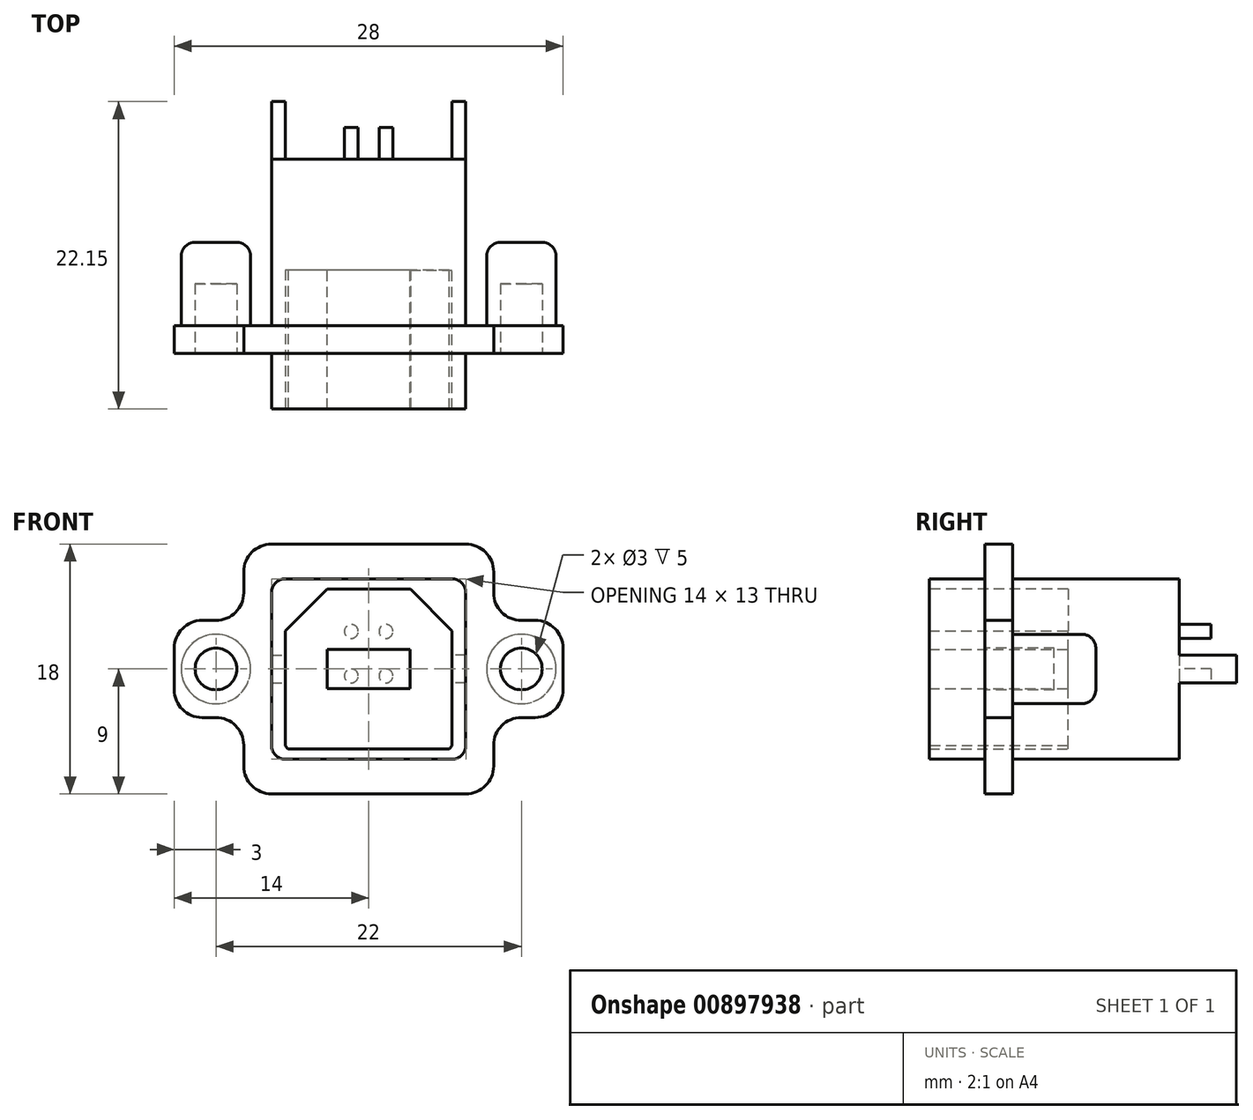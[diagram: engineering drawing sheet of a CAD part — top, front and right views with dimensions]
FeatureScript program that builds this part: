
annotation { "Feature Type Name" : "Feature", "Feature Type Description" : "" }
export const myFeature = defineFeature(function(context is Context, id is Id, definition is map)
    precondition{}
    {
        {
            var Q0;
            Q0=qCreatedBy(makeId("Front.planeOp"),FACE);
            var sketch = newSketch(context, id + "F0", { "sketchPlane" : qUnion([Q0])});
            skLineSegment(sketch, "E0.bottom", {"start": v(9, -9) * mm, "end": v(-9, -9) * mm});
            skLineSegment(sketch, "E0.top", {"start": v(9, 9) * mm, "end": v(-9, 9) * mm});
            skLineSegment(sketch, "E0.left", {"start": v(9, -9) * mm, "end": v(9, 9) * mm});
            skLineSegment(sketch, "E0.right", {"start": v(-9, -9) * mm, "end": v(-9, 9) * mm});
            skPoint(sketch, "E0.middle", {"position": v(0, 0) * mm});
            skLineSegment(sketch, "E1.bottom", {"start": v(-9, 3.5) * mm, "end": v(-14, 3.5) * mm});
            skLineSegment(sketch, "E1.top", {"start": v(-9, -3.5) * mm, "end": v(-14, -3.5) * mm});
            skLineSegment(sketch, "E1.left", {"start": v(-9, 3.5) * mm, "end": v(-9, -3.5) * mm});
            skLineSegment(sketch, "E1.right", {"start": v(-14, 3.5) * mm, "end": v(-14, -3.5) * mm});
            skLineSegment(sketch, "E2.bottom", {"start": v(9, 3.5) * mm, "end": v(14, 3.5) * mm});
            skLineSegment(sketch, "E2.top", {"start": v(9, -3.5) * mm, "end": v(14, -3.5) * mm});
            skLineSegment(sketch, "E2.left", {"start": v(9, 3.5) * mm, "end": v(9, -3.5) * mm});
            skLineSegment(sketch, "E2.right", {"start": v(14, 3.5) * mm, "end": v(14, -3.5) * mm});
            skSolve(sketch);
        }
        {
            var Q0;
            Q0 = qSketchRegion(id + "F0", true);
            extrude(context, id + "F1", {"entities" : qUnion([Q0]), "depth" : 2 * mm, "offsetDistance" : 25 * mm});
        }
        {
            var Q0;
            Q0=makeQuery(id+"F1.opExtrude","CAP_FACE",FACE,{"disambiguationData":[OSD([sQuery(id+"F0.wireOp",EDGE,"E0.bottom"),sQuery(id+"F0.wireOp",EDGE,"E0.top"),sQuery(id+"F0.wireOp",EDGE,"E0.left"),sQuery(id+"F0.wireOp",EDGE,"E0.right"),sQuery(id+"F0.wireOp",EDGE,"E1.bottom"),sQuery(id+"F0.wireOp",EDGE,"E1.top"),sQuery(id+"F0.wireOp",EDGE,"E1.right"),sQuery(id+"F0.wireOp",EDGE,"E2.bottom"),sQuery(id+"F0.wireOp",EDGE,"E2.top"),sQuery(id+"F0.wireOp",EDGE,"E2.right")])],"isStart":false});
            var sketch = newSketch(context, id + "F2", { "sketchPlane" : qUnion([Q0])});
            skLineSegment(sketch, "E3.bottom", {"start": v(7, -6.5) * mm, "end": v(-7, -6.5) * mm});
            skLineSegment(sketch, "E3.top", {"start": v(7, 6.5) * mm, "end": v(-7, 6.5) * mm});
            skLineSegment(sketch, "E3.left", {"start": v(7, -6.5) * mm, "end": v(7, 6.5) * mm});
            skLineSegment(sketch, "E3.right", {"start": v(-7, -6.5) * mm, "end": v(-7, 6.5) * mm});
            skPoint(sketch, "E3.middle", {"position": v(0, 0) * mm});
            skSolve(sketch);
        }
        {
            var Q0;
            Q0 = qSketchRegion(id + "F2", true);
            extrude(context, id + "F3", {"entities" : qUnion([Q0]), "operationType" : NewBodyOperationType.ADD, "depth" : 4 * mm, "offsetDistance" : 25 * mm});
        }
        {
            var Q0;
            Q0=makeQuery(id+"F1.opExtrude","CAP_FACE",FACE,{"disambiguationData":[OSD([sQuery(id+"F0.wireOp",EDGE,"E0.bottom"),sQuery(id+"F0.wireOp",EDGE,"E0.top"),sQuery(id+"F0.wireOp",EDGE,"E0.left"),sQuery(id+"F0.wireOp",EDGE,"E0.right"),sQuery(id+"F0.wireOp",EDGE,"E1.bottom"),sQuery(id+"F0.wireOp",EDGE,"E1.top"),sQuery(id+"F0.wireOp",EDGE,"E1.right"),sQuery(id+"F0.wireOp",EDGE,"E2.bottom"),sQuery(id+"F0.wireOp",EDGE,"E2.top"),sQuery(id+"F0.wireOp",EDGE,"E2.right")])],"isStart":true});
            var sketch = newSketch(context, id + "F4", { "sketchPlane" : qUnion([Q0])});
            skLineSegment(sketch, "E4.bottom", {"start": v(7, -6.5) * mm, "end": v(-7, -6.5) * mm});
            skLineSegment(sketch, "E4.top", {"start": v(7, 6.5) * mm, "end": v(-7, 6.5) * mm});
            skLineSegment(sketch, "E4.left", {"start": v(7, -6.5) * mm, "end": v(7, 6.5) * mm});
            skLineSegment(sketch, "E4.right", {"start": v(-7, -6.5) * mm, "end": v(-7, 6.5) * mm});
            skPoint(sketch, "E4.middle", {"position": v(0, 0) * mm});
            skSolve(sketch);
        }
        {
            var Q0;
            Q0 = qSketchRegion(id + "F4", true);
            extrude(context, id + "F5", {"entities" : qUnion([Q0]), "operationType" : NewBodyOperationType.ADD, "depth" : 12 * mm, "offsetDistance" : 25 * mm});
        }
        {
            var Q0;
            Q0=makeQuery(id+"F1.opExtrude","CAP_FACE",FACE,{"disambiguationData":[OSD([sQuery(id+"F0.wireOp",EDGE,"E0.bottom"),sQuery(id+"F0.wireOp",EDGE,"E0.top"),sQuery(id+"F0.wireOp",EDGE,"E0.left"),sQuery(id+"F0.wireOp",EDGE,"E0.right"),sQuery(id+"F0.wireOp",EDGE,"E1.bottom"),sQuery(id+"F0.wireOp",EDGE,"E1.top"),sQuery(id+"F0.wireOp",EDGE,"E1.right"),sQuery(id+"F0.wireOp",EDGE,"E2.bottom"),sQuery(id+"F0.wireOp",EDGE,"E2.top"),sQuery(id+"F0.wireOp",EDGE,"E2.right")])],"isStart":true});
            var sketch = newSketch(context, id + "F6", { "sketchPlane" : qUnion([Q0])});
            skCircle(sketch, "E5", {"center": v(11, 0) * mm, "radius": 2.5 * mm});
            skCircle(sketch, "E6", {"center": v(-11, 0) * mm, "radius": 2.5 * mm});
            skSolve(sketch);
        }
        {
            var Q0;
            Q0 = qSketchRegion(id + "F6", true);
            extrude(context, id + "F7", {"entities" : qUnion([Q0]), "operationType" : NewBodyOperationType.ADD, "depth" : 6 * mm, "offsetDistance" : 25 * mm});
        }
        {
            var Q0;
            Q0=makeQuery(id+"F1.opExtrude","CAP_FACE",FACE,{"disambiguationData":[OSD([sQuery(id+"F0.wireOp",EDGE,"E0.bottom"),sQuery(id+"F0.wireOp",EDGE,"E0.top"),sQuery(id+"F0.wireOp",EDGE,"E0.left"),sQuery(id+"F0.wireOp",EDGE,"E0.right"),sQuery(id+"F0.wireOp",EDGE,"E1.bottom"),sQuery(id+"F0.wireOp",EDGE,"E1.top"),sQuery(id+"F0.wireOp",EDGE,"E1.right"),sQuery(id+"F0.wireOp",EDGE,"E2.bottom"),sQuery(id+"F0.wireOp",EDGE,"E2.top"),sQuery(id+"F0.wireOp",EDGE,"E2.right")])],"isStart":false});
            var sketch = newSketch(context, id + "F8", { "sketchPlane" : qUnion([Q0])});
            skCircle(sketch, "E7", {"center": v(11, 0) * mm, "radius": 1.5 * mm});
            skCircle(sketch, "E8", {"center": v(-11, 0) * mm, "radius": 1.5 * mm});
            skSolve(sketch);
        }
        {
            var Q0;
            Q0 = qSketchRegion(id + "F8", true);
            extrude(context, id + "F9", {"entities" : qUnion([Q0]), "operationType" : NewBodyOperationType.REMOVE, "oppositeDirection" : true, "depth" : 5 * mm, "offsetDistance" : 25 * mm});
        }
        {
            var Q0;
            Q0=makeQuery(id+"F1.opExtrude","SWEPT_EDGE",EDGE,{"disambiguationData":[OSD([sQuery(id+"F0.wireOp",EDGE,"E0.top"),sQuery(id+"F0.wireOp",EDGE,"E0.left")])]});
            var Q1;
            Q1=makeQuery(id+"F1.opExtrude","SWEPT_EDGE",EDGE,{"disambiguationData":[OSD([sQuery(id+"F0.wireOp",EDGE,"E0.top"),sQuery(id+"F0.wireOp",EDGE,"E0.right")])]});
            var Q2;
            Q2=makeQuery(id+"F1.opExtrude","SWEPT_EDGE",EDGE,{"disambiguationData":[OSD([sQuery(id+"F0.wireOp",EDGE,"E0.left"),sQuery(id+"F0.wireOp",EDGE,"E2.bottom"),sQuery(id+"F0.wireOp",EDGE,"E2.left")])]});
            var Q3;
            Q3=makeQuery(id+"F1.opExtrude","SWEPT_EDGE",EDGE,{"disambiguationData":[OSD([sQuery(id+"F0.wireOp",EDGE,"E2.bottom"),sQuery(id+"F0.wireOp",EDGE,"E2.right")])]});
            var Q4;
            Q4=makeQuery(id+"F1.opExtrude","SWEPT_EDGE",EDGE,{"disambiguationData":[OSD([sQuery(id+"F0.wireOp",EDGE,"E2.top"),sQuery(id+"F0.wireOp",EDGE,"E2.right")])]});
            var Q5;
            Q5=makeQuery(id+"F1.opExtrude","SWEPT_EDGE",EDGE,{"disambiguationData":[OSD([sQuery(id+"F0.wireOp",EDGE,"E0.left"),sQuery(id+"F0.wireOp",EDGE,"E2.top"),sQuery(id+"F0.wireOp",EDGE,"E2.left")])]});
            var Q6;
            Q6=makeQuery(id+"F1.opExtrude","SWEPT_EDGE",EDGE,{"disambiguationData":[OSD([sQuery(id+"F0.wireOp",EDGE,"E0.bottom"),sQuery(id+"F0.wireOp",EDGE,"E0.left")])]});
            var Q7;
            Q7=makeQuery(id+"F1.opExtrude","SWEPT_EDGE",EDGE,{"disambiguationData":[OSD([sQuery(id+"F0.wireOp",EDGE,"E0.bottom"),sQuery(id+"F0.wireOp",EDGE,"E0.right")])]});
            var Q8;
            Q8=makeQuery(id+"F1.opExtrude","SWEPT_EDGE",EDGE,{"disambiguationData":[OSD([sQuery(id+"F0.wireOp",EDGE,"E0.right"),sQuery(id+"F0.wireOp",EDGE,"E1.top"),sQuery(id+"F0.wireOp",EDGE,"E1.left")])]});
            var Q9;
            Q9=makeQuery(id+"F1.opExtrude","SWEPT_EDGE",EDGE,{"disambiguationData":[OSD([sQuery(id+"F0.wireOp",EDGE,"E1.top"),sQuery(id+"F0.wireOp",EDGE,"E1.right")])]});
            var Q10;
            Q10=makeQuery(id+"F1.opExtrude","SWEPT_EDGE",EDGE,{"disambiguationData":[OSD([sQuery(id+"F0.wireOp",EDGE,"E1.bottom"),sQuery(id+"F0.wireOp",EDGE,"E1.right")])]});
            var Q11;
            Q11=makeQuery(id+"F1.opExtrude","SWEPT_EDGE",EDGE,{"disambiguationData":[OSD([sQuery(id+"F0.wireOp",EDGE,"E0.right"),sQuery(id+"F0.wireOp",EDGE,"E1.bottom"),sQuery(id+"F0.wireOp",EDGE,"E1.left")])]});
            fillet(context, id + "F10", {"entities" : qUnion([Q0, Q1, Q2, Q3, Q4, Q5, Q6, Q7, Q8, Q9, Q10, Q11]), "radius" : 2 * mm, "tangentPropagation" : true, "allowEdgeOverflow" : false});
        }
        {
            var Q0;
            Q0=makeQuery(id+"F3.opExtrude","SWEPT_EDGE",EDGE,{"disambiguationData":[OSD([sQuery(id+"F2.wireOp",EDGE,"E3.top"),sQuery(id+"F2.wireOp",EDGE,"E3.left")])]});
            var Q1;
            Q1=makeQuery(id+"F3.opExtrude","SWEPT_EDGE",EDGE,{"disambiguationData":[OSD([sQuery(id+"F2.wireOp",EDGE,"E3.top"),sQuery(id+"F2.wireOp",EDGE,"E3.right")])]});
            var Q2;
            Q2=makeQuery(id+"F3.opExtrude","SWEPT_EDGE",EDGE,{"disambiguationData":[OSD([sQuery(id+"F2.wireOp",EDGE,"E3.bottom"),sQuery(id+"F2.wireOp",EDGE,"E3.left")])]});
            var Q3;
            Q3=makeQuery(id+"F3.opExtrude","SWEPT_EDGE",EDGE,{"disambiguationData":[OSD([sQuery(id+"F2.wireOp",EDGE,"E3.bottom"),sQuery(id+"F2.wireOp",EDGE,"E3.right")])]});
            var Q4;
            Q4=makeQuery(id+"F5.opExtrude","SWEPT_EDGE",EDGE,{"disambiguationData":[OSD([sQuery(id+"F4.wireOp",EDGE,"E4.top"),sQuery(id+"F4.wireOp",EDGE,"E4.right")])]});
            var Q5;
            Q5=makeQuery(id+"F5.opExtrude","SWEPT_EDGE",EDGE,{"disambiguationData":[OSD([sQuery(id+"F4.wireOp",EDGE,"E4.top"),sQuery(id+"F4.wireOp",EDGE,"E4.left")])]});
            var Q6;
            Q6=makeQuery(id+"F5.opExtrude","SWEPT_EDGE",EDGE,{"disambiguationData":[OSD([sQuery(id+"F4.wireOp",EDGE,"E4.bottom"),sQuery(id+"F4.wireOp",EDGE,"E4.right")])]});
            var Q7;
            Q7=makeQuery(id+"F5.opExtrude","SWEPT_EDGE",EDGE,{"disambiguationData":[OSD([sQuery(id+"F4.wireOp",EDGE,"E4.bottom"),sQuery(id+"F4.wireOp",EDGE,"E4.left")])]});
            fillet(context, id + "F11", {"entities" : qUnion([Q0, Q1, Q2, Q3, Q4, Q5, Q6, Q7]), "radius" : 1 * mm, "tangentPropagation" : true, "allowEdgeOverflow" : false});
        }
        {
            var Q0;
            Q0=makeQuery(id+"F7.opExtrude","CAP_EDGE",EDGE,{"disambiguationData":[OSD([sQuery(id+"F6.wireOp",EDGE,"E6")])],"isStart":false});
            var Q1;
            Q1=makeQuery(id+"F7.opExtrude","CAP_EDGE",EDGE,{"disambiguationData":[OSD([sQuery(id+"F6.wireOp",EDGE,"E5")])],"isStart":false});
            var Q2;
            Q2=makeQuery(id+"F7.opExtrude","CAP_EDGE",EDGE,{"disambiguationData":[OSD([sQuery(id+"F6.wireOp",EDGE,"E6")])],"isStart":true});
            var Q3;
            Q3=makeQuery(id+"F7.opExtrude","CAP_EDGE",EDGE,{"disambiguationData":[OSD([sQuery(id+"F6.wireOp",EDGE,"E5")])],"isStart":true});
            fillet(context, id + "F12", {"entities" : qUnion([Q0, Q1, Q2, Q3]), "radius" : 1 * mm, "tangentPropagation" : true, "allowEdgeOverflow" : false});
        }
        {
            var Q0;
            Q0=makeQuery(id+"F3.opExtrude","CAP_FACE",FACE,{"disambiguationData":[OSD([sQuery(id+"F2.wireOp",EDGE,"E3.bottom"),sQuery(id+"F2.wireOp",EDGE,"E3.top"),sQuery(id+"F2.wireOp",EDGE,"E3.left"),sQuery(id+"F2.wireOp",EDGE,"E3.right")])],"isStart":false});
            var sketch = newSketch(context, id + "F13", { "sketchPlane" : qUnion([Q0])});
            skLineSegment(sketch, "E9.bottom", {"start": v(6, -5.75) * mm, "end": v(-6, -5.75) * mm});
            skLineSegment(sketch, "E9.top", {"start": v(6, 5.75) * mm, "end": v(-6, 5.75) * mm});
            skLineSegment(sketch, "E9.left", {"start": v(6, -5.75) * mm, "end": v(6, 5.75) * mm});
            skLineSegment(sketch, "E9.right", {"start": v(-6, -5.75) * mm, "end": v(-6, 5.75) * mm});
            skPoint(sketch, "E9.middle", {"position": v(0, 0) * mm});
            skSolve(sketch);
        }
        {
            var Q0;
            Q0 = qSketchRegion(id + "F13", true);
            extrude(context, id + "F14", {"entities" : qUnion([Q0]), "operationType" : NewBodyOperationType.REMOVE, "oppositeDirection" : true, "depth" : 10 * mm, "offsetDistance" : 25 * mm});
        }
        {
            var Q0;
            Q0=makeQuery(id+"F14.boolean.opBoolean","COPY",EDGE,{"derivedFrom":makeQuery(id+"F14.opExtrude","SWEPT_EDGE",EDGE,{"disambiguationData":[OSD([sQuery(id+"F13.wireOp",EDGE,"E9.bottom"),sQuery(id+"F13.wireOp",EDGE,"E9.left")])]})});
            var Q1;
            Q1=makeQuery(id+"F14.boolean.opBoolean","COPY",EDGE,{"derivedFrom":makeQuery(id+"F14.opExtrude","SWEPT_EDGE",EDGE,{"disambiguationData":[OSD([sQuery(id+"F13.wireOp",EDGE,"E9.bottom"),sQuery(id+"F13.wireOp",EDGE,"E9.right")])]})});
            chamfer(context, id + "F15", {"entities" : qUnion([Q0, Q1]), "width" : 0.2 * mm, "tangentPropagation" : true});
        }
        {
            var Q0;
            Q0=makeQuery(id+"F14.boolean.opBoolean","COPY",EDGE,{"derivedFrom":makeQuery(id+"F14.opExtrude","SWEPT_EDGE",EDGE,{"disambiguationData":[OSD([sQuery(id+"F13.wireOp",EDGE,"E9.top"),sQuery(id+"F13.wireOp",EDGE,"E9.right")])]})});
            var Q1;
            Q1=makeQuery(id+"F14.boolean.opBoolean","COPY",EDGE,{"derivedFrom":makeQuery(id+"F14.opExtrude","SWEPT_EDGE",EDGE,{"disambiguationData":[OSD([sQuery(id+"F13.wireOp",EDGE,"E9.top"),sQuery(id+"F13.wireOp",EDGE,"E9.left")])]})});
            chamfer(context, id + "F16", {"entities" : qUnion([Q0, Q1]), "width" : 3 * mm, "tangentPropagation" : true});
        }
        {
            var Q0;
            Q0=makeQuery(id+"F14.boolean.opBoolean","COPY",FACE,{"derivedFrom":makeQuery(id+"F14.opExtrude","CAP_FACE",FACE,{"disambiguationData":[OSD([sQuery(id+"F13.wireOp",EDGE,"E9.bottom"),sQuery(id+"F13.wireOp",EDGE,"E9.top"),sQuery(id+"F13.wireOp",EDGE,"E9.left"),sQuery(id+"F13.wireOp",EDGE,"E9.right")])],"isStart":false})});
            var sketch = newSketch(context, id + "F17", { "sketchPlane" : qUnion([Q0])});
            skLineSegment(sketch, "E10.bottom", {"start": v(2.97, -1.42) * mm, "end": v(-2.97, -1.42) * mm});
            skLineSegment(sketch, "E10.top", {"start": v(2.97, 1.42) * mm, "end": v(-2.97, 1.42) * mm});
            skLineSegment(sketch, "E10.left", {"start": v(2.97, -1.42) * mm, "end": v(2.97, 1.42) * mm});
            skLineSegment(sketch, "E10.right", {"start": v(-2.97, -1.42) * mm, "end": v(-2.97, 1.42) * mm});
            skPoint(sketch, "E10.middle", {"position": v(0, 0) * mm});
            skSolve(sketch);
        }
        {
            var Q0;
            Q0 = qSketchRegion(id + "F17", true);
            extrude(context, id + "F18", {"entities" : qUnion([Q0]), "operationType" : NewBodyOperationType.ADD, "depth" : 10 * mm, "offsetDistance" : 25 * mm});
        }
        {
            var Q0;
            Q0=makeQuery(id+"F5.opExtrude","CAP_FACE",FACE,{"disambiguationData":[OSD([sQuery(id+"F4.wireOp",EDGE,"E4.bottom"),sQuery(id+"F4.wireOp",EDGE,"E4.top"),sQuery(id+"F4.wireOp",EDGE,"E4.left"),sQuery(id+"F4.wireOp",EDGE,"E4.right")])],"isStart":false});
            var sketch = newSketch(context, id + "F19", { "sketchPlane" : qUnion([Q0])});
            skLineSegment(sketch, "E11.bottom", {"start": v(-7, 1) * mm, "end": v(-6, 1) * mm});
            skLineSegment(sketch, "E11.top", {"start": v(-7, -1) * mm, "end": v(-6, -1) * mm});
            skLineSegment(sketch, "E11.left", {"start": v(-7, 1) * mm, "end": v(-7, -1) * mm});
            skLineSegment(sketch, "E11.right", {"start": v(-6, 1) * mm, "end": v(-6, -1) * mm});
            skLineSegment(sketch, "E12.bottom", {"start": v(7, 1) * mm, "end": v(6, 1) * mm});
            skLineSegment(sketch, "E12.top", {"start": v(7, -1) * mm, "end": v(6, -1) * mm});
            skLineSegment(sketch, "E12.left", {"start": v(7, 1) * mm, "end": v(7, -1) * mm});
            skLineSegment(sketch, "E12.right", {"start": v(6, 1) * mm, "end": v(6, -1) * mm});
            skSolve(sketch);
        }
        {
            var Q0;
            Q0 = qSketchRegion(id + "F19", true);
            extrude(context, id + "F20", {"entities" : qUnion([Q0]), "operationType" : NewBodyOperationType.ADD, "depth" : 4.15 * mm, "offsetDistance" : 25 * mm});
        }
        {
            var Q0;
            Q0=makeQuery(id+"F5.opExtrude","CAP_FACE",FACE,{"disambiguationData":[OSD([sQuery(id+"F4.wireOp",EDGE,"E4.bottom"),sQuery(id+"F4.wireOp",EDGE,"E4.top"),sQuery(id+"F4.wireOp",EDGE,"E4.left"),sQuery(id+"F4.wireOp",EDGE,"E4.right")])],"isStart":false});
            var sketch = newSketch(context, id + "F21", { "sketchPlane" : qUnion([Q0])});
            skCircle(sketch, "E13", {"center": v(1.25, 2.7) * mm, "radius": 0.5 * mm});
            skCircle(sketch, "E14", {"center": v(-1.25, 2.7) * mm, "radius": 0.5 * mm});
            skCircle(sketch, "E15", {"center": v(1.25, -0.5) * mm, "radius": 0.5 * mm});
            skCircle(sketch, "E16", {"center": v(-1.25, -0.5) * mm, "radius": 0.5 * mm});
            skSolve(sketch);
        }
        {
            var Q0;
            Q0 = qSketchRegion(id + "F21", true);
            extrude(context, id + "F22", {"entities" : qUnion([Q0]), "operationType" : NewBodyOperationType.ADD, "depth" : 2.3 * mm, "offsetDistance" : 25 * mm});
        }
    });
